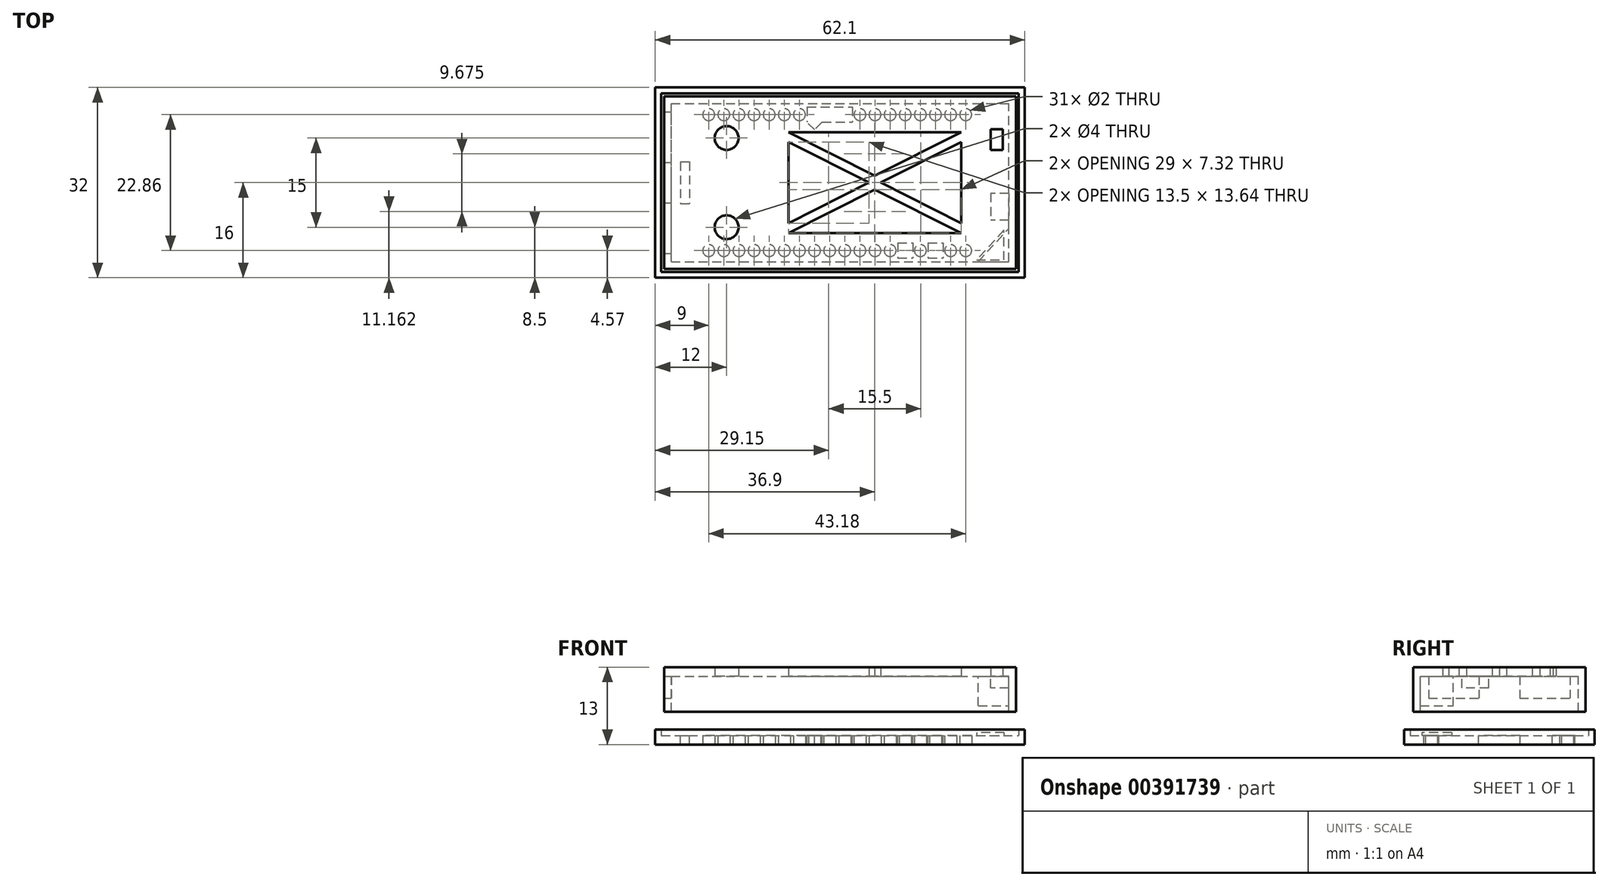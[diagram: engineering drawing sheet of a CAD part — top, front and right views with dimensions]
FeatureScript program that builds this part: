
annotation { "Feature Type Name" : "Feature", "Feature Type Description" : "" }
export const myFeature = defineFeature(function(context is Context, id is Id, definition is map)
    precondition{}
    {
        {
            var Q0;
            Q0=qCreatedBy(makeId("Top.planeOp"),FACE);
            var sketch = newSketch(context, id + "F0", { "sketchPlane" : qUnion([Q0])});
            skLineSegment(sketch, "E0", {"start": v(0, 0) * mm, "end": v(51, 0) * mm});
            skLineSegment(sketch, "E1", {"start": v(51, 0) * mm, "end": v(55.6, 5) * mm});
            skLineSegment(sketch, "E2", {"start": v(55.6, 5) * mm, "end": v(55.6, 26) * mm});
            skLineSegment(sketch, "E3", {"start": v(55.6, 26) * mm, "end": v(0, 26) * mm});
            skLineSegment(sketch, "E4", {"start": v(0, 26) * mm, "end": v(0, 24.9) * mm});
            skLineSegment(sketch, "E5", {"start": v(0, 24.9) * mm, "end": v(-1.3, 24.9) * mm});
            skLineSegment(sketch, "E6", {"start": v(-1.3, 24.9) * mm, "end": v(-1.3, 16.4) * mm});
            skLineSegment(sketch, "E7", {"start": v(-1.3, 16.4) * mm, "end": v(0, 16.4) * mm});
            skLineSegment(sketch, "E8", {"start": v(0, 16.4) * mm, "end": v(0, 9.6) * mm});
            skLineSegment(sketch, "E9", {"start": v(0, 9.6) * mm, "end": v(-1.3, 9.6) * mm});
            skLineSegment(sketch, "E10", {"start": v(-1.3, 9.6) * mm, "end": v(-1.3, 1.1) * mm});
            skLineSegment(sketch, "E11", {"start": v(-1.3, 1.1) * mm, "end": v(0, 1.1) * mm});
            skLineSegment(sketch, "E12", {"start": v(0, 1.1) * mm, "end": v(0, 0) * mm});
            skSolve(sketch);
        }
        {
            var Q0;
            Q0=qCreatedBy(makeId("Top.planeOp"),FACE);
            var sketch = newSketch(context, id + "F1", { "sketchPlane" : qUnion([Q0])});
            skLineSegment(sketch, "E13.bottom", {"start": v(-1.5, -1.5) * mm, "end": v(57.6, -1.5) * mm});
            skLineSegment(sketch, "E13.top", {"start": v(-1.5, 27.5) * mm, "end": v(57.6, 27.5) * mm});
            skLineSegment(sketch, "E13.left", {"start": v(-1.5, -1.5) * mm, "end": v(-1.5, 27.5) * mm});
            skLineSegment(sketch, "E13.right", {"start": v(57.6, -1.5) * mm, "end": v(57.6, 27.5) * mm});
            skSolve(sketch);
        }
        {
            var Q0;
            Q0 = qSketchRegion(id + "F1", true);
            extrude(context, id + "F2", {"entities" : qUnion([Q0]), "depth" : 1.5 * mm});
        }
        {
            var Q0;
            Q0=makeQuery(id+"F0.imprint","IMPRINT",FACE,{"disambiguationData":[TD([[makeQuery(id+"F0.imprint","IMPRINT",EDGE,{"derivedFrom":sQuery(id+"F0.wireOp",EDGE,"E0")}),1.0]])]});
            var sketch = newSketch(context, id + "F3", { "sketchPlane" : qUnion([Q0])});
            skLineSegment(sketch, "E14.bottom", {"start": v(-1.5, -1.5) * mm, "end": v(57.6, -1.5) * mm});
            skLineSegment(sketch, "E14.top", {"start": v(-1.5, 27.5) * mm, "end": v(57.6, 27.5) * mm});
            skLineSegment(sketch, "E14.left", {"start": v(-1.5, -1.5) * mm, "end": v(-1.5, 27.5) * mm});
            skLineSegment(sketch, "E14.right", {"start": v(57.6, -1.5) * mm, "end": v(57.6, 27.5) * mm});
            skLineSegment(sketch, "E15.0", {"start": v(-0.3, 26.3) * mm, "end": v(56.4, 26.3) * mm});
            skLineSegment(sketch, "E15.1", {"start": v(-0.3, -0.3) * mm, "end": v(-0.3, 26.3) * mm});
            skLineSegment(sketch, "E15.2", {"start": v(-0.3, -0.3) * mm, "end": v(56.4, -0.3) * mm});
            skLineSegment(sketch, "E15.3", {"start": v(56.4, -0.3) * mm, "end": v(56.4, 26.3) * mm});
            skSolve(sketch);
        }
        {
            var Q0;
            Q0 = qSketchRegion(id + "F3", true);
            extrude(context, id + "F4", {"entities" : qUnion([Q0]), "operationType" : NewBodyOperationType.ADD, "oppositeDirection" : true, "depth" : 6 * mm});
        }
        {
            var Q0;
            Q0=makeQuery(id+"F2.opExtrude","CAP_FACE",FACE,{"disambiguationData":[OSD([sQuery(id+"F1.wireOp",EDGE,"E13.bottom"),sQuery(id+"F1.wireOp",EDGE,"E13.top"),sQuery(id+"F1.wireOp",EDGE,"E13.left"),sQuery(id+"F1.wireOp",EDGE,"E13.right")])],"isStart":true});
            var sketch = newSketch(context, id + "F5", { "sketchPlane" : qUnion([Q0])});
            skLineSegment(sketch, "E16", {"start": v(56.4, 0.3) * mm, "end": v(51.27, 0.3) * mm});
            skLineSegment(sketch, "E17", {"start": v(51.27, 0.3) * mm, "end": v(56.4, -5.28) * mm});
            skLineSegment(sketch, "E18", {"start": v(56.4, -5.28) * mm, "end": v(56.4, 0.3) * mm});
            skSolve(sketch);
        }
        {
            var Q0;
            Q0 = qSketchRegion(id + "F5", true);
            extrude(context, id + "F6", {"entities" : qUnion([Q0]), "operationType" : NewBodyOperationType.ADD, "depth" : 5 * mm});
        }
        {
            var Q0;
            Q0=makeQuery(id+"F4.opExtrude","SWEPT_FACE",FACE,{"disambiguationData":[OSD([sQuery(id+"F3.wireOp",EDGE,"E15.1")])]});
            var sketch = newSketch(context, id + "F7", { "sketchPlane" : qUnion([Q0])});
            skLineSegment(sketch, "E19.bottom", {"start": v(1.1, 0) * mm, "end": v(9.6, 0) * mm});
            skLineSegment(sketch, "E19.top", {"start": v(1.1, -3.7) * mm, "end": v(9.6, -3.7) * mm});
            skLineSegment(sketch, "E19.left", {"start": v(1.1, 0) * mm, "end": v(1.1, -3.7) * mm});
            skLineSegment(sketch, "E19.right", {"start": v(9.6, 0) * mm, "end": v(9.6, -3.7) * mm});
            skLineSegment(sketch, "E20.bottom", {"start": v(16.4, 0) * mm, "end": v(24.9, 0) * mm});
            skLineSegment(sketch, "E20.top", {"start": v(16.4, -3.7) * mm, "end": v(24.9, -3.7) * mm});
            skLineSegment(sketch, "E20.left", {"start": v(16.4, 0) * mm, "end": v(16.4, -3.7) * mm});
            skLineSegment(sketch, "E20.right", {"start": v(24.9, 0) * mm, "end": v(24.9, -3.7) * mm});
            skSolve(sketch);
        }
        {
            var Q0;
            Q0 = qSketchRegion(id + "F7", true);
            extrude(context, id + "F8", {"entities" : qUnion([Q0]), "operationType" : NewBodyOperationType.REMOVE, "endBound" : BoundingType.UP_TO_NEXT, "oppositeDirection" : true, "depth" : 25 * mm});
        }
        {
            var Q0;
            Q0=makeQuery(id+"F0.imprint","IMPRINT",FACE,{"disambiguationData":[TD([[makeQuery(id+"F0.imprint","IMPRINT",EDGE,{"derivedFrom":sQuery(id+"F0.wireOp",EDGE,"E0")}),1.0]])]});
            var sketch = newSketch(context, id + "F9", { "sketchPlane" : qUnion([Q0])});
            skCircle(sketch, "E21", {"center": v(9, 5.5) * mm, "radius": 2 * mm});
            skCircle(sketch, "E22", {"center": v(9, 20.5) * mm, "radius": 2 * mm});
            skSolve(sketch);
        }
        {
            var Q0;
            Q0 = qSketchRegion(id + "F9", true);
            extrude(context, id + "F10", {"entities" : qUnion([Q0]), "operationType" : NewBodyOperationType.REMOVE, "endBound" : BoundingType.UP_TO_NEXT, "depth" : 25 * mm});
        }
        {
            var Q0;
            Q0=makeQuery(id+"F0.imprint","IMPRINT",FACE,{"disambiguationData":[TD([[makeQuery(id+"F0.imprint","IMPRINT",EDGE,{"derivedFrom":sQuery(id+"F0.wireOp",EDGE,"E0")}),1.0]])]});
            var sketch = newSketch(context, id + "F11", { "sketchPlane" : qUnion([Q0])});
            skLineSegment(sketch, "E23", {"start": v(19.4, 4.5) * mm, "end": v(48.4, 4.5) * mm});
            skLineSegment(sketch, "E24", {"start": v(48.4, 4.5) * mm, "end": v(33.9, 11.82) * mm});
            skLineSegment(sketch, "E25", {"start": v(33.9, 11.82) * mm, "end": v(19.4, 4.5) * mm});
            skLineSegment(sketch, "E26", {"start": v(19.4, 6.18) * mm, "end": v(32.9, 13) * mm});
            skLineSegment(sketch, "E27", {"start": v(32.9, 13) * mm, "end": v(19.4, 19.82) * mm});
            skLineSegment(sketch, "E28", {"start": v(19.4, 19.82) * mm, "end": v(19.4, 6.18) * mm});
            skLineSegment(sketch, "E29", {"start": v(19.4, 21.5) * mm, "end": v(48.4, 21.5) * mm});
            skLineSegment(sketch, "E30", {"start": v(48.4, 21.5) * mm, "end": v(33.9, 14.18) * mm});
            skLineSegment(sketch, "E31", {"start": v(33.9, 14.18) * mm, "end": v(19.4, 21.5) * mm});
            skLineSegment(sketch, "E32", {"start": v(48.4, 6.18) * mm, "end": v(48.4, 19.82) * mm});
            skLineSegment(sketch, "E33", {"start": v(48.4, 19.82) * mm, "end": v(34.9, 13) * mm});
            skLineSegment(sketch, "E34", {"start": v(34.9, 13) * mm, "end": v(48.4, 6.18) * mm});
            skPoint(sketch, "E35", {"position": v(19.4, 13) * mm});
            skLineSegment(sketch, "E36.bottom", {"start": v(53.4, 18.5) * mm, "end": v(55.4, 18.5) * mm});
            skLineSegment(sketch, "E36.top", {"start": v(53.4, 22) * mm, "end": v(55.4, 22) * mm});
            skLineSegment(sketch, "E36.left", {"start": v(53.4, 18.5) * mm, "end": v(53.4, 22) * mm});
            skLineSegment(sketch, "E36.right", {"start": v(55.4, 18.5) * mm, "end": v(55.4, 22) * mm});
            skSolve(sketch);
        }
        {
            var Q0;
            Q0 = qSketchRegion(id + "F11", true);
            extrude(context, id + "F12", {"entities" : qUnion([Q0]), "operationType" : NewBodyOperationType.REMOVE, "endBound" : BoundingType.UP_TO_NEXT, "depth" : 25 * mm});
        }
        {
            var Q0;
            Q0=qCreatedBy(makeId("Top.planeOp"),FACE);
            cPlane(context, id + "F13", {"entities" : qUnion([Q0]), "cplaneType" : CPlaneType.OFFSET, "offset" : 10 * mm, "oppositeDirection" : true, "width" : 150 * mm, "height" : 150 * mm});
        }
        {
            var Q0;
            Q0=qCreatedBy(id+"F13.planeOp",FACE);
            var sketch = newSketch(context, id + "F14", { "sketchPlane" : qUnion([Q0])});
            skLineSegment(sketch, "E37.0", {"start": v(-3, -3) * mm, "end": v(59.1, -3) * mm});
            skLineSegment(sketch, "E37.1", {"start": v(-3, -3) * mm, "end": v(-3, 29) * mm});
            skLineSegment(sketch, "E37.2", {"start": v(-3, 29) * mm, "end": v(59.1, 29) * mm});
            skLineSegment(sketch, "E37.3", {"start": v(59.1, -3) * mm, "end": v(59.1, 29) * mm});
            skSolve(sketch);
        }
        {
            var Q0;
            Q0 = qSketchRegion(id + "F14", true);
            extrude(context, id + "F15", {"entities" : qUnion([Q0]), "oppositeDirection" : true, "depth" : 1.5 * mm});
        }
        {
            var Q0;
            Q0=makeQuery(id+"F15.opExtrude","CAP_FACE",FACE,{"disambiguationData":[OSD([sQuery(id+"F14.wireOp",EDGE,"E37.0"),sQuery(id+"F14.wireOp",EDGE,"E37.1"),sQuery(id+"F14.wireOp",EDGE,"E37.2"),sQuery(id+"F14.wireOp",EDGE,"E37.3")])],"isStart":true});
            var sketch = newSketch(context, id + "F16", { "sketchPlane" : qUnion([Q0])});
            skLineSegment(sketch, "E38.0", {"start": v(-3, -3) * mm, "end": v(-3, 29) * mm});
            skLineSegment(sketch, "E38.1", {"start": v(-3, -3) * mm, "end": v(59.1, -3) * mm});
            skLineSegment(sketch, "E38.2", {"start": v(59.1, -3) * mm, "end": v(59.1, 29) * mm});
            skLineSegment(sketch, "E38.3", {"start": v(-3, 29) * mm, "end": v(59.1, 29) * mm});
            skLineSegment(sketch, "E39.0", {"start": v(-2, 28) * mm, "end": v(58.1, 28) * mm});
            skLineSegment(sketch, "E39.1", {"start": v(-2, -2) * mm, "end": v(-2, 28) * mm});
            skLineSegment(sketch, "E39.2", {"start": v(-2, -2) * mm, "end": v(58.1, -2) * mm});
            skLineSegment(sketch, "E39.3", {"start": v(58.1, -2) * mm, "end": v(58.1, 28) * mm});
            skSolve(sketch);
        }
        {
            var Q0;
            Q0 = qSketchRegion(id + "F16", true);
            extrude(context, id + "F17", {"entities" : qUnion([Q0]), "operationType" : NewBodyOperationType.ADD, "depth" : 1 * mm});
        }
        {
            var Q0;
            Q0=makeQuery(id+"F15.opExtrude","CAP_FACE",FACE,{"disambiguationData":[OSD([sQuery(id+"F14.wireOp",EDGE,"E37.0"),sQuery(id+"F14.wireOp",EDGE,"E37.1"),sQuery(id+"F14.wireOp",EDGE,"E37.2"),sQuery(id+"F14.wireOp",EDGE,"E37.3")])],"isStart":false});
            var sketch = newSketch(context, id + "F18", { "sketchPlane" : qUnion([Q0])});
            skCircle(sketch, "E40", {"center": v(6, -24.43) * mm, "radius": 1 * mm});
            skCircle(sketch, "E41", {"center": v(6, -1.57) * mm, "radius": 1 * mm});
            skLineSegment(sketch, "E42", {"start": v(6, -1.57) * mm, "end": v(6, -24.43) * mm, "construction": true});
            skPoint(sketch, "E43", {"position": v(6, -13) * mm});
            skCircle(sketch, "E44.1.0.0", {"center": v(8.54, -24.43) * mm, "radius": 1 * mm});
            skCircle(sketch, "E44.1.0.1", {"center": v(8.54, -1.57) * mm, "radius": 1 * mm});
            skCircle(sketch, "E44.2.0.0", {"center": v(11.08, -24.43) * mm, "radius": 1 * mm});
            skCircle(sketch, "E44.2.0.1", {"center": v(11.08, -1.57) * mm, "radius": 1 * mm});
            skLineSegment(sketch, "E44.direction1", {"start": v(6, -24.43) * mm, "end": v(8.54, -24.43) * mm, "construction": true});
            skCircle(sketch, "E45.0.3.0", {"center": v(13.62, -24.43) * mm, "radius": 1 * mm});
            skCircle(sketch, "E45.2.3.0", {"center": v(13.62, -1.57) * mm, "radius": 1 * mm});
            skCircle(sketch, "E45.0.4.0", {"center": v(16.16, -24.43) * mm, "radius": 1 * mm});
            skCircle(sketch, "E45.2.4.0", {"center": v(16.16, -1.57) * mm, "radius": 1 * mm});
            skCircle(sketch, "E45.0.5.0", {"center": v(18.7, -24.43) * mm, "radius": 1 * mm});
            skCircle(sketch, "E45.2.5.0", {"center": v(18.7, -1.57) * mm, "radius": 1 * mm});
            skCircle(sketch, "E45.0.6.0", {"center": v(21.24, -24.43) * mm, "radius": 1 * mm});
            skCircle(sketch, "E45.2.6.0", {"center": v(21.24, -1.57) * mm, "radius": 1 * mm});
            skCircle(sketch, "E45.0.7.0", {"center": v(23.78, -24.43) * mm, "radius": 1 * mm});
            skCircle(sketch, "E45.2.7.0", {"center": v(23.78, -1.57) * mm, "radius": 1 * mm});
            skCircle(sketch, "E45.0.8.0", {"center": v(26.32, -24.43) * mm, "radius": 1 * mm});
            skCircle(sketch, "E45.2.8.0", {"center": v(26.32, -1.57) * mm, "radius": 1 * mm});
            skCircle(sketch, "E45.0.9.0", {"center": v(28.86, -24.43) * mm, "radius": 1 * mm});
            skCircle(sketch, "E45.2.9.0", {"center": v(28.86, -1.57) * mm, "radius": 1 * mm});
            skCircle(sketch, "E45.0.10.0", {"center": v(31.4, -24.43) * mm, "radius": 1 * mm});
            skCircle(sketch, "E45.2.10.0", {"center": v(31.4, -1.57) * mm, "radius": 1 * mm});
            skCircle(sketch, "E45.0.11.0", {"center": v(33.94, -24.43) * mm, "radius": 1 * mm});
            skCircle(sketch, "E45.2.11.0", {"center": v(33.94, -1.57) * mm, "radius": 1 * mm});
            skCircle(sketch, "E45.0.12.0", {"center": v(36.48, -24.43) * mm, "radius": 1 * mm});
            skCircle(sketch, "E45.2.12.0", {"center": v(36.48, -1.57) * mm, "radius": 1 * mm});
            skCircle(sketch, "E45.0.13.0", {"center": v(39.02, -24.43) * mm, "radius": 1 * mm});
            skCircle(sketch, "E45.2.13.0", {"center": v(39.02, -1.57) * mm, "radius": 1 * mm});
            skCircle(sketch, "E45.0.14.0", {"center": v(41.56, -24.43) * mm, "radius": 1 * mm});
            skCircle(sketch, "E45.2.14.0", {"center": v(41.56, -1.57) * mm, "radius": 1 * mm});
            skCircle(sketch, "E45.0.15.0", {"center": v(44.1, -24.43) * mm, "radius": 1 * mm});
            skCircle(sketch, "E45.2.15.0", {"center": v(44.1, -1.57) * mm, "radius": 1 * mm});
            skCircle(sketch, "E45.0.16.0", {"center": v(46.64, -24.43) * mm, "radius": 1 * mm});
            skCircle(sketch, "E45.2.16.0", {"center": v(46.64, -1.57) * mm, "radius": 1 * mm});
            skCircle(sketch, "E45.0.17.0", {"center": v(49.18, -24.43) * mm, "radius": 1 * mm});
            skCircle(sketch, "E45.2.17.0", {"center": v(49.18, -1.57) * mm, "radius": 1 * mm});
            skSolve(sketch);
        }
        {
            var Q0;
            Q0 = qSketchRegion(id + "F18", true);
            extrude(context, id + "F19", {"entities" : qUnion([Q0]), "operationType" : NewBodyOperationType.REMOVE, "endBound" : BoundingType.UP_TO_NEXT, "oppositeDirection" : true, "depth" : 25 * mm});
        }
        {
            var Q0;
            Q0=makeQuery(id+"F0.imprint","IMPRINT",FACE,{"disambiguationData":[TD([[makeQuery(id+"F0.imprint","IMPRINT",EDGE,{"derivedFrom":sQuery(id+"F0.wireOp",EDGE,"E0")}),1.0]])]});
            var sketch = newSketch(context, id + "F20", { "sketchPlane" : qUnion([Q0])});
            skLineSegment(sketch, "E46.bottom", {"start": v(56.4, 11.2) * mm, "end": v(53.4, 11.2) * mm});
            skLineSegment(sketch, "E46.top", {"start": v(56.4, 6.7) * mm, "end": v(53.4, 6.7) * mm});
            skLineSegment(sketch, "E46.left", {"start": v(56.4, 11.2) * mm, "end": v(56.4, 6.7) * mm});
            skLineSegment(sketch, "E46.right", {"start": v(53.4, 11.2) * mm, "end": v(53.4, 6.7) * mm});
            skSolve(sketch);
        }
        {
            var Q0;
            Q0 = qSketchRegion(id + "F20", true);
            extrude(context, id + "F21", {"entities" : qUnion([Q0]), "operationType" : NewBodyOperationType.ADD, "oppositeDirection" : true, "depth" : 2 * mm});
        }
        {
            var Q0;
            Q0=makeQuery(id+"F15.opExtrude","CAP_FACE",FACE,{"disambiguationData":[OSD([sQuery(id+"F14.wireOp",EDGE,"E37.0"),sQuery(id+"F14.wireOp",EDGE,"E37.1"),sQuery(id+"F14.wireOp",EDGE,"E37.2"),sQuery(id+"F14.wireOp",EDGE,"E37.3")])],"isStart":true});
            var sketch = newSketch(context, id + "F22", { "sketchPlane" : qUnion([Q0])});
            skLineSegment(sketch, "E47", {"start": v(51, 0) * mm, "end": v(55.6, 0) * mm});
            skLineSegment(sketch, "E48", {"start": v(55.6, 0) * mm, "end": v(55.6, 5) * mm});
            skLineSegment(sketch, "E49", {"start": v(55.6, 5) * mm, "end": v(51, 0) * mm});
            skSolve(sketch);
        }
        {
            var Q0;
            Q0 = qSketchRegion(id + "F22", true);
            extrude(context, id + "F23", {"entities" : qUnion([Q0]), "operationType" : NewBodyOperationType.ADD, "depth" : 0.5 * mm});
        }
        {
            var Q0;
            Q0=makeQuery(id+"F15.opExtrude","CAP_FACE",FACE,{"disambiguationData":[OSD([sQuery(id+"F14.wireOp",EDGE,"E37.0"),sQuery(id+"F14.wireOp",EDGE,"E37.1"),sQuery(id+"F14.wireOp",EDGE,"E37.2"),sQuery(id+"F14.wireOp",EDGE,"E37.3")])],"isStart":true});
            var sketch = newSketch(context, id + "F24", { "sketchPlane" : qUnion([Q0])});
            skLineSegment(sketch, "E50.bottom", {"start": v(42.83, 2.84) * mm, "end": v(45.37, 2.84) * mm});
            skLineSegment(sketch, "E50.top", {"start": v(42.83, 0.3) * mm, "end": v(45.37, 0.3) * mm});
            skLineSegment(sketch, "E50.left", {"start": v(42.83, 2.84) * mm, "end": v(42.83, 0.3) * mm});
            skLineSegment(sketch, "E50.right", {"start": v(45.37, 2.84) * mm, "end": v(45.37, 0.3) * mm});
            skLineSegment(sketch, "E51.bottom", {"start": v(37.75, 2.84) * mm, "end": v(40.29, 2.84) * mm});
            skLineSegment(sketch, "E51.top", {"start": v(37.75, 0.3) * mm, "end": v(40.29, 0.3) * mm});
            skLineSegment(sketch, "E51.left", {"start": v(37.75, 2.84) * mm, "end": v(37.75, 0.3) * mm});
            skLineSegment(sketch, "E51.right", {"start": v(40.29, 2.84) * mm, "end": v(40.29, 0.3) * mm});
            skLineSegment(sketch, "E52.bottom", {"start": v(27.59, 25.7) * mm, "end": v(30.13, 25.7) * mm});
            skLineSegment(sketch, "E52.top", {"start": v(27.59, 23.16) * mm, "end": v(30.13, 23.16) * mm});
            skLineSegment(sketch, "E52.left", {"start": v(27.59, 25.7) * mm, "end": v(27.59, 23.16) * mm});
            skLineSegment(sketch, "E52.right", {"start": v(30.13, 25.7) * mm, "end": v(30.13, 23.16) * mm});
            skLineSegment(sketch, "E53.bottom", {"start": v(25.05, 25.7) * mm, "end": v(27.59, 25.7) * mm});
            skLineSegment(sketch, "E53.top", {"start": v(25.05, 23.16) * mm, "end": v(27.59, 23.16) * mm});
            skLineSegment(sketch, "E53.left", {"start": v(25.05, 25.7) * mm, "end": v(25.05, 23.16) * mm});
            skLineSegment(sketch, "E54.bottom", {"start": v(22.5, 25.7) * mm, "end": v(25.05, 25.7) * mm});
            skLineSegment(sketch, "E54.left", {"start": v(22.5, 25.7) * mm, "end": v(22.5, 23.16) * mm});
            skPoint(sketch, "E55", {"position": v(44.1, 1.57) * mm});
            skPoint(sketch, "E56", {"position": v(39.02, 1.57) * mm});
            skPoint(sketch, "E57", {"position": v(28.86, 24.43) * mm});
            skPoint(sketch, "E58", {"position": v(26.32, 24.43) * mm});
            skPoint(sketch, "E59", {"position": v(23.78, 24.43) * mm});
            skPoint(sketch, "E60", {"position": v(44.1, 2.84) * mm});
            skPoint(sketch, "E61", {"position": v(42.83, 1.57) * mm});
            skPoint(sketch, "E62", {"position": v(39.02, 2.84) * mm});
            skPoint(sketch, "E63", {"position": v(37.75, 1.57) * mm});
            skPoint(sketch, "E64", {"position": v(28.86, 25.7) * mm});
            skPoint(sketch, "E65", {"position": v(26.32, 25.7) * mm});
            skPoint(sketch, "E66", {"position": v(23.78, 25.7) * mm});
            skPoint(sketch, "E67", {"position": v(22.5, 24.43) * mm});
            skPoint(sketch, "E68", {"position": v(25.05, 24.43) * mm});
            skPoint(sketch, "E69", {"position": v(27.59, 24.43) * mm});
            skLineSegment(sketch, "E70", {"start": v(25.05, 23.16) * mm, "end": v(23.78, 21.9) * mm});
            skLineSegment(sketch, "E71", {"start": v(23.78, 21.91) * mm, "end": v(22.5, 23.16) * mm});
            skSolve(sketch);
        }
        {
            var Q0;
            Q0 = qSketchRegion(id + "F24", true);
            var Q1;
            Q1=makeQuery(id+"F15.opExtrude","CAP_FACE",FACE,{"disambiguationData":[OSD([sQuery(id+"F14.wireOp",EDGE,"E37.0"),sQuery(id+"F14.wireOp",EDGE,"E37.1"),sQuery(id+"F14.wireOp",EDGE,"E37.2"),sQuery(id+"F14.wireOp",EDGE,"E37.3")])],"isStart":false});
            extrude(context, id + "F25", {"entities" : qUnion([Q0]), "operationType" : NewBodyOperationType.REMOVE, "endBound" : BoundingType.UP_TO_SURFACE, "oppositeDirection" : true, "endBoundEntityFace" : qUnion([Q1]), "depth" : 25 * mm});
        }
        {
            var Q0;
            Q0=makeQuery(id+"F15.opExtrude","CAP_FACE",FACE,{"disambiguationData":[OSD([sQuery(id+"F14.wireOp",EDGE,"E37.0"),sQuery(id+"F14.wireOp",EDGE,"E37.1"),sQuery(id+"F14.wireOp",EDGE,"E37.2"),sQuery(id+"F14.wireOp",EDGE,"E37.3")])],"isStart":true});
            var sketch = newSketch(context, id + "F26", { "sketchPlane" : qUnion([Q0])});
            skLineSegment(sketch, "E72.bottom", {"start": v(1.25, 16.5) * mm, "end": v(2.75, 16.5) * mm});
            skLineSegment(sketch, "E72.top", {"start": v(1.25, 9.5) * mm, "end": v(2.75, 9.5) * mm});
            skLineSegment(sketch, "E72.left", {"start": v(1.25, 16.5) * mm, "end": v(1.25, 9.5) * mm});
            skLineSegment(sketch, "E72.right", {"start": v(2.75, 16.5) * mm, "end": v(2.75, 9.5) * mm});
            skPoint(sketch, "E73", {"position": v(1.25, 13) * mm});
            skSolve(sketch);
        }
        {
            var Q0;
            Q0 = qSketchRegion(id + "F26", true);
            extrude(context, id + "F27", {"entities" : qUnion([Q0]), "operationType" : NewBodyOperationType.REMOVE, "endBound" : BoundingType.UP_TO_NEXT, "oppositeDirection" : true, "depth" : 25 * mm});
        }
    });
